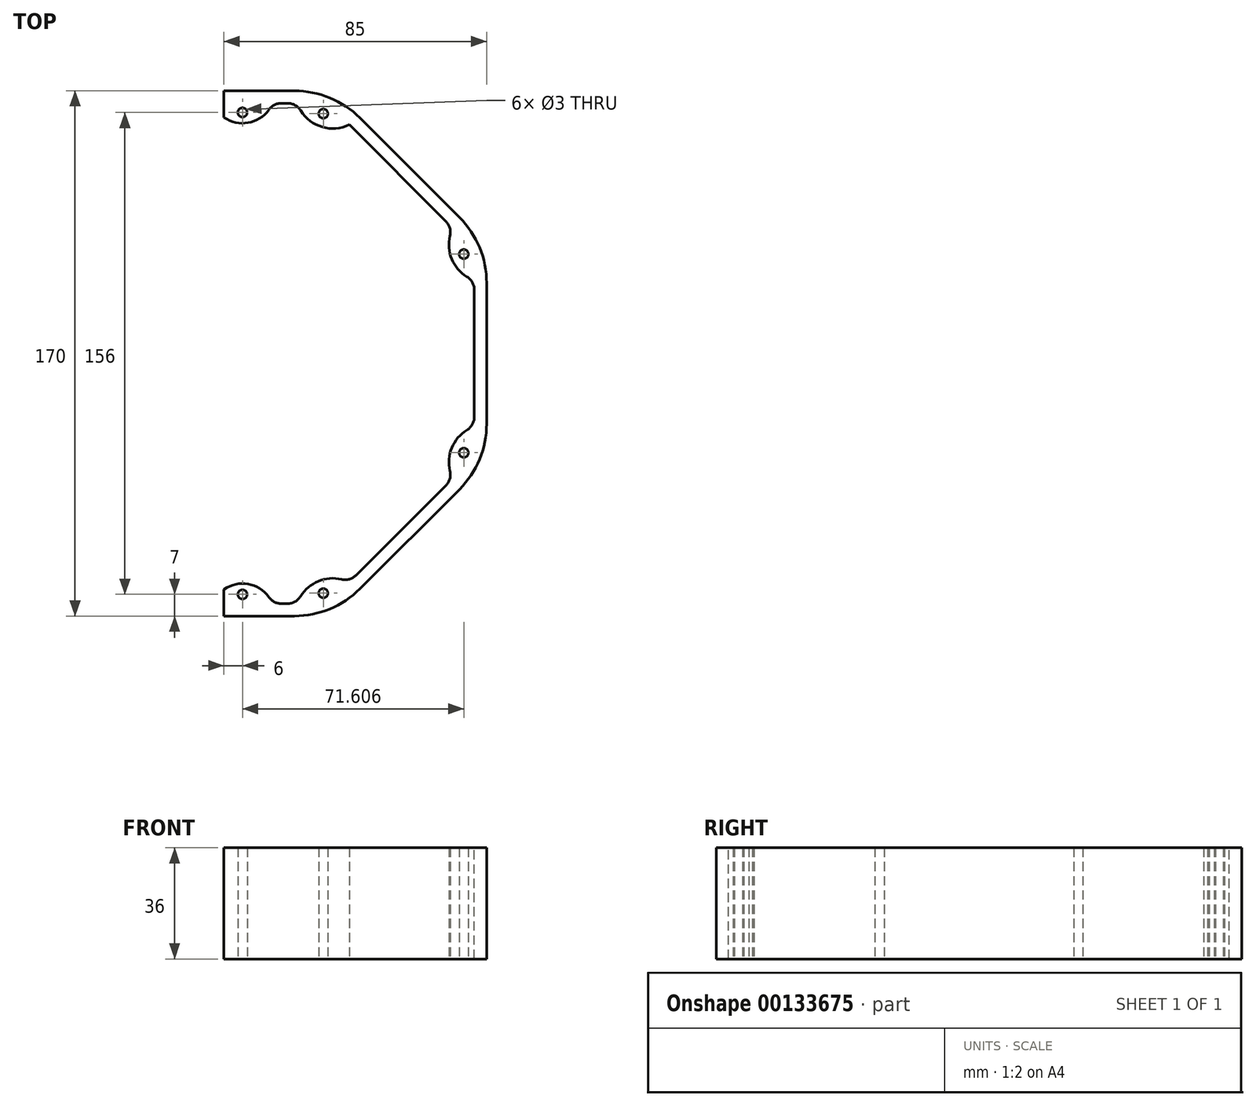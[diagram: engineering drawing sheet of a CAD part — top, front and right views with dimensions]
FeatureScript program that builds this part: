
annotation { "Feature Type Name" : "Feature", "Feature Type Description" : "" }
export const myFeature = defineFeature(function(context is Context, id is Id, definition is map)
    precondition{}
    {
        {
            var Q0;
            Q0=qCreatedBy(makeId("Top.planeOp"),FACE);
            var sketch = newSketch(context, id + "F0", { "sketchPlane" : qUnion([Q0])});
            skCircle(sketch, "E0.cCircle", {"center": v(0, 0) * mm, "radius": 85 * mm, "construction": true});
            skLineSegment(sketch, "E0.0", {"start": v(-85, -35.2) * mm, "end": v(-85, 35.2) * mm});
            skLineSegment(sketch, "E0.1", {"start": v(-85, 35.2) * mm, "end": v(-35.2, 85) * mm});
            skLineSegment(sketch, "E0.2", {"start": v(-35.2, 85) * mm, "end": v(35.2, 85) * mm});
            skLineSegment(sketch, "E0.3", {"start": v(35.2, 85) * mm, "end": v(85, 35.2) * mm});
            skLineSegment(sketch, "E0.4", {"start": v(85, 35.2) * mm, "end": v(85, -35.2) * mm});
            skLineSegment(sketch, "E0.5", {"start": v(85, -35.2) * mm, "end": v(35.2, -85) * mm});
            skLineSegment(sketch, "E0.6", {"start": v(35.2, -85) * mm, "end": v(-35.2, -85) * mm});
            skLineSegment(sketch, "E0.7", {"start": v(-35.2, -85) * mm, "end": v(-85, -35.2) * mm});
            skPoint(sketch, "E0.0.midPoint", {"position": v(-85, 0) * mm});
            skLineSegment(sketch, "E1.0", {"start": v(-81, -33.55) * mm, "end": v(-81, 33.55) * mm});
            skLineSegment(sketch, "E1.1", {"start": v(-33.55, -81) * mm, "end": v(-81, -33.55) * mm});
            skLineSegment(sketch, "E1.2", {"start": v(-81, 33.55) * mm, "end": v(-33.55, 81) * mm});
            skLineSegment(sketch, "E1.3", {"start": v(33.55, -81) * mm, "end": v(-33.55, -81) * mm});
            skLineSegment(sketch, "E1.4", {"start": v(-33.55, 81) * mm, "end": v(33.55, 81) * mm});
            skLineSegment(sketch, "E1.5", {"start": v(33.55, 81) * mm, "end": v(81, 33.55) * mm});
            skLineSegment(sketch, "E1.6", {"start": v(81, 33.55) * mm, "end": v(81, -33.55) * mm});
            skLineSegment(sketch, "E1.7", {"start": v(81, -33.55) * mm, "end": v(33.55, -81) * mm});
            skLineSegment(sketch, "E2", {"start": v(0, 81) * mm, "end": v(0, 85) * mm});
            skLineSegment(sketch, "E3", {"start": v(-35.2, -85) * mm, "end": v(-33.55, -81) * mm});
            skLineSegment(sketch, "E4", {"start": v(35.2, -85) * mm, "end": v(33.55, -81) * mm});
            skLineSegment(sketch, "E5", {"start": v(-85, 0) * mm, "end": v(85, 0) * mm, "construction": true});
            skLineSegment(sketch, "E6", {"start": v(0, -81) * mm, "end": v(0, -85) * mm});
            skLineSegment(sketch, "E7", {"start": v(0, 0) * mm, "end": v(-85, 35.2) * mm, "construction": true});
            skCircle(sketch, "E8", {"center": v(-77.6, 32.15) * mm, "radius": 1.5 * mm});
            skArc(sketch, "E9.trimOffspring", {"start": v(-81.7, 23.46) * mm, "mid": v(-73.73, 30.54) * mm, "end": v(-74.36, 41.18) * mm});
            skCircle(sketch, "E10.1.0", {"center": v(-77.6, -32.15) * mm, "radius": 1.5 * mm});
            skArc(sketch, "E10.1.1", {"start": v(-74.36, -41.18) * mm, "mid": v(-73.73, -30.54) * mm, "end": v(-81.7, -23.46) * mm});
            skCircle(sketch, "E10.2.0", {"center": v(-32.15, -77.6) * mm, "radius": 1.5 * mm});
            skArc(sketch, "E10.2.1", {"start": v(-23.46, -81.7) * mm, "mid": v(-30.54, -73.73) * mm, "end": v(-41.18, -74.36) * mm});
            skCircle(sketch, "E10.3.0", {"center": v(32.15, -77.6) * mm, "radius": 1.5 * mm});
            skArc(sketch, "E10.3.1", {"start": v(41.18, -74.36) * mm, "mid": v(30.54, -73.73) * mm, "end": v(23.46, -81.7) * mm});
            skCircle(sketch, "E10.4.0", {"center": v(77.6, -32.15) * mm, "radius": 1.5 * mm});
            skArc(sketch, "E10.4.1", {"start": v(81.7, -23.46) * mm, "mid": v(73.73, -30.54) * mm, "end": v(74.36, -41.18) * mm});
            skCircle(sketch, "E10.5.0", {"center": v(77.6, 32.15) * mm, "radius": 1.5 * mm});
            skArc(sketch, "E10.5.1", {"start": v(74.36, 41.18) * mm, "mid": v(73.73, 30.54) * mm, "end": v(81.7, 23.46) * mm});
            skCircle(sketch, "E10.6.0", {"center": v(32.15, 77.6) * mm, "radius": 1.5 * mm});
            skArc(sketch, "E10.6.1", {"start": v(23.46, 81.7) * mm, "mid": v(30.54, 73.73) * mm, "end": v(41.18, 74.36) * mm});
            skCircle(sketch, "E10.7.0", {"center": v(-32.15, 77.6) * mm, "radius": 1.5 * mm});
            skArc(sketch, "E10.7.1", {"start": v(-41.18, 74.36) * mm, "mid": v(-30.54, 73.73) * mm, "end": v(-23.46, 81.7) * mm});
            skLineSegment(sketch, "E11", {"start": v(0, 0) * mm, "end": v(0, 78) * mm});
            skLineSegment(sketch, "E12", {"start": v(0, 78) * mm, "end": v(-6, 78) * mm});
            skLineSegment(sketch, "E13", {"start": v(0, 78) * mm, "end": v(6, 78) * mm});
            skCircle(sketch, "E14", {"center": v(-6, 78) * mm, "radius": 1.5 * mm});
            skCircle(sketch, "E15", {"center": v(6, 78) * mm, "radius": 1.5 * mm});
            skArc(sketch, "E16", {"start": v(-16.38, 83.4) * mm, "mid": v(-5.26, 74.53) * mm, "end": v(4.5, 84.88) * mm});
            skArc(sketch, "E17", {"start": v(-4.5, 84.88) * mm, "mid": v(5.26, 74.53) * mm, "end": v(16.38, 83.4) * mm});
            skLineSegment(sketch, "E18", {"start": v(0, 78) * mm, "end": v(0, 81) * mm});
            skArc(sketch, "E19.1.0", {"start": v(16.38, -83.4) * mm, "mid": v(5.26, -74.53) * mm, "end": v(-4.5, -84.88) * mm});
            skArc(sketch, "E19.1.1", {"start": v(4.5, -84.88) * mm, "mid": v(-5.26, -74.53) * mm, "end": v(-16.38, -83.4) * mm});
            skCircle(sketch, "E19.1.2", {"center": v(-6, -78) * mm, "radius": 1.5 * mm});
            skCircle(sketch, "E19.1.3", {"center": v(6, -78) * mm, "radius": 1.5 * mm});
            skLineSegment(sketch, "E20", {"start": v(0, -81) * mm, "end": v(0, -76.38) * mm});
            skSolve(sketch);
        }
        {
            var Q0;
            {var subQ0=sQuery(id+"F0.wireOp",EDGE,"E18");Q0=makeQuery(id+"F0.imprint","IMPRINT",FACE,{"disambiguationData":[TD([[makeQuery(id+"F0.imprint","IMPRINT",EDGE,{"derivedFrom":subQ0}),-1.0]])]});}
            var Q1;
            {var subQ0=sQuery(id+"F0.wireOp",EDGE,"E13");var subQ3=sQuery(id+"F0.wireOp",EDGE,"E16");var subQ5=makeQuery(id+"F0.imprint","INTERSECT",VERTEX,{"derivedFrom":[subQ0,subQ3]});Q1=makeQuery(id+"F0.imprint","IMPRINT",FACE,{"disambiguationData":[TD([[makeQuery(id+"F0.imprint","IMPRINT",EDGE,{"disambiguationData":[TD([[subQ5,1.0]])],"derivedFrom":subQ3}),1.0]])]});}
            var Q2;
            Q2=makeQuery(id+"F0.imprint","IMPRINT",FACE,{"disambiguationData":[TD([[makeQuery(id+"F0.imprint","IMPRINT",EDGE,{"derivedFrom":sQuery(id+"F0.wireOp",EDGE,"E15")}),-1.0]])]});
            var Q3;
            {var subQ12=sQuery(id+"F0.wireOp",EDGE,"E0.3");Q3=makeQuery(id+"F0.imprint","IMPRINT",FACE,{"disambiguationData":[TD([[makeQuery(id+"F0.imprint","IMPRINT",EDGE,{"derivedFrom":subQ12}),-1.0]])]});}
            var Q4;
            Q4=makeQuery(id+"F0.imprint","IMPRINT",FACE,{"disambiguationData":[TD([[makeQuery(id+"F0.imprint","IMPRINT",EDGE,{"derivedFrom":sQuery(id+"F0.wireOp",EDGE,"E10.6.0")}),-1.0]])]});
            var Q5;
            Q5=makeQuery(id+"F0.imprint","IMPRINT",FACE,{"disambiguationData":[TD([[makeQuery(id+"F0.imprint","IMPRINT",EDGE,{"derivedFrom":sQuery(id+"F0.wireOp",EDGE,"E10.5.0")}),-1.0]])]});
            var Q6;
            Q6=makeQuery(id+"F0.imprint","IMPRINT",FACE,{"disambiguationData":[TD([[makeQuery(id+"F0.imprint","IMPRINT",EDGE,{"derivedFrom":sQuery(id+"F0.wireOp",EDGE,"E10.4.0")}),-1.0]])]});
            var Q7;
            Q7=makeQuery(id+"F0.imprint","IMPRINT",FACE,{"disambiguationData":[TD([[makeQuery(id+"F0.imprint","IMPRINT",EDGE,{"derivedFrom":sQuery(id+"F0.wireOp",EDGE,"E10.3.0")}),-1.0]])]});
            var Q8;
            {var subQ3=sQuery(id+"F0.wireOp",EDGE,"E4");Q8=makeQuery(id+"F0.imprint","IMPRINT",FACE,{"disambiguationData":[TD([[makeQuery(id+"F0.imprint","IMPRINT",EDGE,{"derivedFrom":subQ3}),1.0]])]});}
            var Q9;
            Q9=makeQuery(id+"F0.imprint","IMPRINT",FACE,{"disambiguationData":[TD([[makeQuery(id+"F0.imprint","IMPRINT",EDGE,{"derivedFrom":sQuery(id+"F0.wireOp",EDGE,"E19.1.3")}),-1.0]])]});
            var Q10;
            {var subQ0=sQuery(id+"F0.wireOp",EDGE,"E20");Q10=makeQuery(id+"F0.imprint","IMPRINT",FACE,{"disambiguationData":[TD([[makeQuery(id+"F0.imprint","IMPRINT",EDGE,{"derivedFrom":subQ0}),-1.0]])]});}
            extrude(context, id + "F1", {"entities" : qUnion([Q0, Q1, Q2, Q3, Q4, Q5, Q6, Q7, Q8, Q9, Q10]), "depth" : 36 * mm});
        }
        {
            var Q0;
            Q0=makeQuery(id+"F1.opExtrude","SWEPT_EDGE",EDGE,{"disambiguationData":[OSD([sQuery(id+"F0.wireOp",EDGE,"E0.4"),sQuery(id+"F0.wireOp",EDGE,"E0.5")])]});
            var Q1;
            Q1=makeQuery(id+"F1.opExtrude","SWEPT_EDGE",EDGE,{"disambiguationData":[OSD([sQuery(id+"F0.wireOp",EDGE,"E0.3"),sQuery(id+"F0.wireOp",EDGE,"E0.4")])]});
            var Q2;
            Q2=makeQuery(id+"F1.opExtrude","SWEPT_EDGE",EDGE,{"disambiguationData":[OSD([sQuery(id+"F0.wireOp",EDGE,"E0.2"),sQuery(id+"F0.wireOp",EDGE,"E0.3")])]});
            var Q3;
            Q3=makeQuery(id+"F1.opExtrude","SWEPT_EDGE",EDGE,{"disambiguationData":[OSD([sQuery(id+"F0.wireOp",EDGE,"E0.5"),sQuery(id+"F0.wireOp",EDGE,"E0.6"),sQuery(id+"F0.wireOp",EDGE,"E4")])]});
            fillet(context, id + "F2", {"entities" : qUnion([Q0, Q1, Q2, Q3]), "radius" : 30 * mm, "tangentPropagation" : true, "allowEdgeOverflow" : false});
        }
        {
            var Q0;
            Q0=makeQuery(id+"F1.opExtrude","SWEPT_EDGE",EDGE,{"disambiguationData":[OSD([sQuery(id+"F0.wireOp",EDGE,"E1.4"),sQuery(id+"F0.wireOp",EDGE,"E10.6.1")])]});
            var Q1;
            Q1=makeQuery(id+"F1.opExtrude","SWEPT_EDGE",EDGE,{"disambiguationData":[OSD([sQuery(id+"F0.wireOp",EDGE,"E1.4"),sQuery(id+"F0.wireOp",EDGE,"E17")])]});
            var Q2;
            Q2=makeQuery(id+"F1.opExtrude","SWEPT_EDGE",EDGE,{"disambiguationData":[OSD([sQuery(id+"F0.wireOp",EDGE,"E1.5"),sQuery(id+"F0.wireOp",EDGE,"E10.5.1")])]});
            var Q3;
            Q3=makeQuery(id+"F1.opExtrude","SWEPT_EDGE",EDGE,{"disambiguationData":[OSD([sQuery(id+"F0.wireOp",EDGE,"E1.6"),sQuery(id+"F0.wireOp",EDGE,"E10.5.1")])]});
            var Q4;
            Q4=makeQuery(id+"F1.opExtrude","SWEPT_EDGE",EDGE,{"disambiguationData":[OSD([sQuery(id+"F0.wireOp",EDGE,"E1.6"),sQuery(id+"F0.wireOp",EDGE,"E10.4.1")])]});
            var Q5;
            Q5=makeQuery(id+"F1.opExtrude","SWEPT_EDGE",EDGE,{"disambiguationData":[OSD([sQuery(id+"F0.wireOp",EDGE,"E1.7"),sQuery(id+"F0.wireOp",EDGE,"E10.4.1")])]});
            var Q6;
            Q6=makeQuery(id+"F1.opExtrude","SWEPT_EDGE",EDGE,{"disambiguationData":[OSD([sQuery(id+"F0.wireOp",EDGE,"E1.7"),sQuery(id+"F0.wireOp",EDGE,"E10.3.1")])]});
            var Q7;
            Q7=makeQuery(id+"F1.opExtrude","SWEPT_EDGE",EDGE,{"disambiguationData":[OSD([sQuery(id+"F0.wireOp",EDGE,"E1.3"),sQuery(id+"F0.wireOp",EDGE,"E19.1.0")])]});
            var Q8;
            Q8=makeQuery(id+"F1.opExtrude","SWEPT_EDGE",EDGE,{"disambiguationData":[OSD([sQuery(id+"F0.wireOp",EDGE,"E1.3"),sQuery(id+"F0.wireOp",EDGE,"E10.3.1")])]});
            fillet(context, id + "F3", {"entities" : qUnion([Q0, Q1, Q2, Q3, Q4, Q5, Q6, Q7, Q8]), "radius" : 5 * mm, "tangentPropagation" : true, "allowEdgeOverflow" : false});
        }
    });
